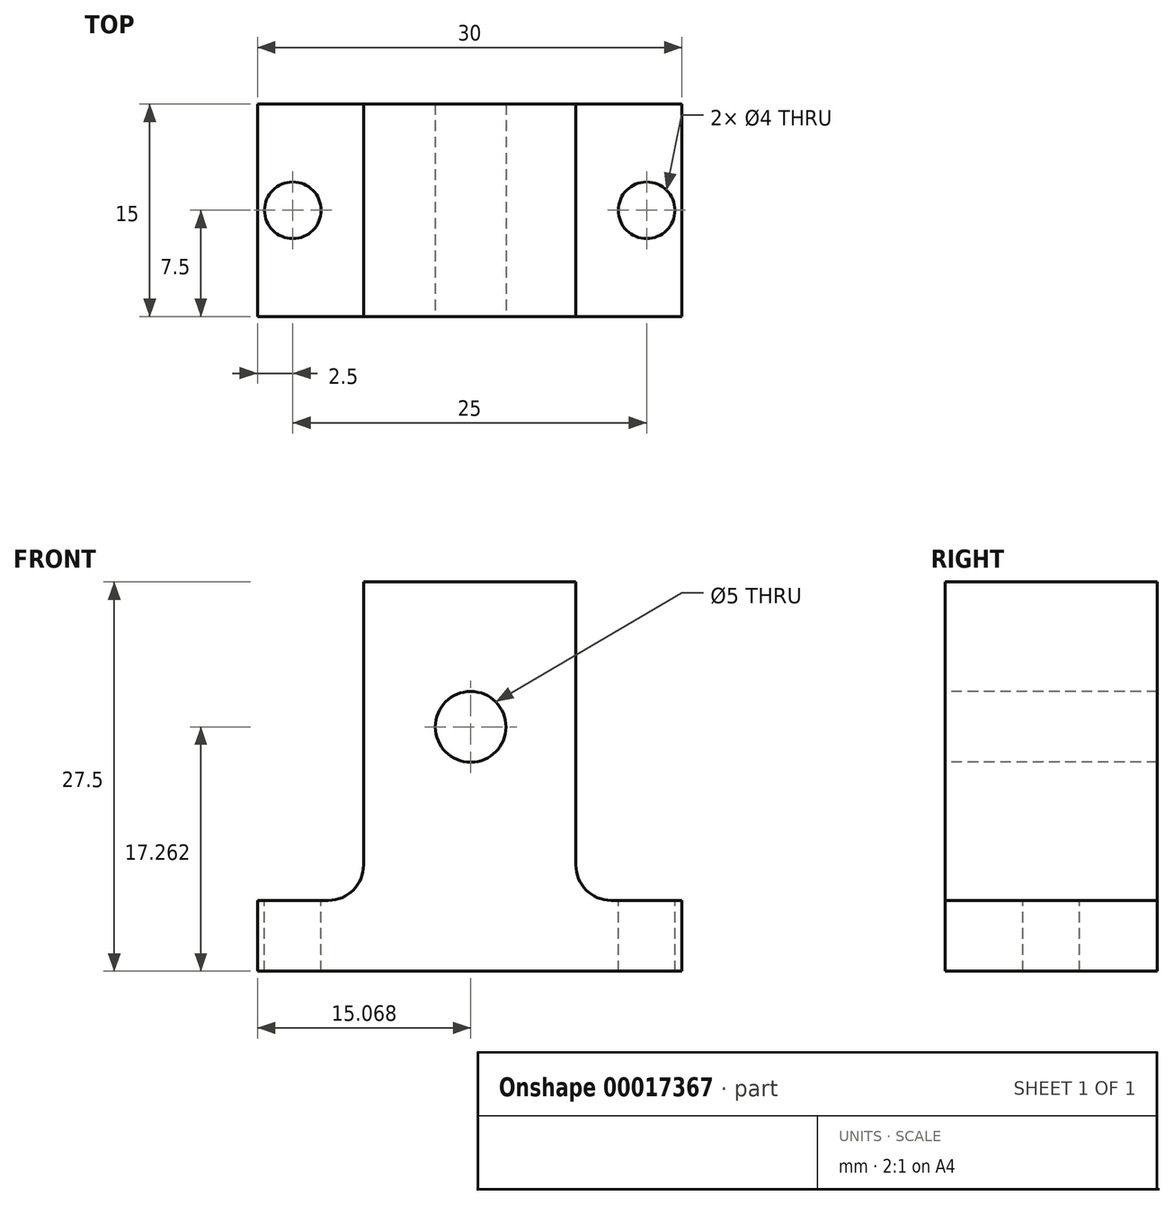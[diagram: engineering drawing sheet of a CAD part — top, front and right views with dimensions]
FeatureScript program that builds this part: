
annotation { "Feature Type Name" : "Feature", "Feature Type Description" : "" }
export const myFeature = defineFeature(function(context is Context, id is Id, definition is map)
    precondition{}
    {
        {
            var Q0;
            Q0=qCreatedBy(makeId("Front.planeOp"),FACE);
            var sketch = newSketch(context, id + "F0", { "sketchPlane" : qUnion([Q0])});
            skLineSegment(sketch, "E0", {"start": v(-35, -18.2) * mm, "end": v(-5, -18.2) * mm});
            skLineSegment(sketch, "E1", {"start": v(-5, -18.2) * mm, "end": v(-5, -13.2) * mm});
            skLineSegment(sketch, "E2", {"start": v(-35, -18.2) * mm, "end": v(-35, -13.2) * mm});
            skLineSegment(sketch, "E3", {"start": v(-35, -13.2) * mm, "end": v(-30, -13.2) * mm});
            skLineSegment(sketch, "E4", {"start": v(-5, -13.2) * mm, "end": v(-10, -13.2) * mm});
            skLineSegment(sketch, "E5", {"start": v(-12.5, -10.7) * mm, "end": v(-12.5, 9.3) * mm});
            skLineSegment(sketch, "E6", {"start": v(-27.5, -10.7) * mm, "end": v(-27.5, 9.3) * mm});
            skPoint(sketch, "E7.visualSharp", {"position": v(-27.5, -13.2) * mm});
            skArc(sketch, "E7.filletArc", {"start": v(-30, -13.2) * mm, "mid": v(-28.23, -12.48) * mm, "end": v(-27.5, -10.7) * mm});
            skPoint(sketch, "E8.visualSharp", {"position": v(-12.5, -13.2) * mm});
            skArc(sketch, "E8.filletArc", {"start": v(-12.5, -10.7) * mm, "mid": v(-11.77, -12.48) * mm, "end": v(-10, -13.2) * mm});
            skLineSegment(sketch, "E9", {"start": v(-27.5, 9.3) * mm, "end": v(-12.5, 9.3) * mm});
            skSolve(sketch);
        }
        {
            var Q0;
            Q0=makeQuery(id+"F0.imprint","IMPRINT",FACE,{"disambiguationData":[TD([[makeQuery(id+"F0.imprint","IMPRINT",EDGE,{"derivedFrom":sQuery(id+"F0.wireOp",EDGE,"E0")}),1.0]])]});
            extrude(context, id + "F1", {"entities" : qUnion([Q0]), "depth" : 15 * mm});
        }
        {
            var Q0;
            Q0=makeQuery(id+"F1.opExtrude","CAP_FACE",FACE,{"disambiguationData":[OSD([sQuery(id+"F0.wireOp",EDGE,"E0"),sQuery(id+"F0.wireOp",EDGE,"E1"),sQuery(id+"F0.wireOp",EDGE,"E2"),sQuery(id+"F0.wireOp",EDGE,"E3"),sQuery(id+"F0.wireOp",EDGE,"E4"),sQuery(id+"F0.wireOp",EDGE,"E5"),sQuery(id+"F0.wireOp",EDGE,"E6"),sQuery(id+"F0.wireOp",EDGE,"E7.filletArc"),sQuery(id+"F0.wireOp",EDGE,"E8.filletArc"),sQuery(id+"F0.wireOp",EDGE,"E9")])],"isStart":false});
            var sketch = newSketch(context, id + "F2", { "sketchPlane" : qUnion([Q0])});
            skSolve(sketch);
        }
        {
            var Q0;
            Q0=makeQuery(id+"F2.imprint","IMPRINT",FACE,{"disambiguationData":[TD([[makeQuery(id+"F2.imprint","IMPRINT",EDGE,{"derivedFrom":makeQuery(id+"F1.opExtrude","CAP_EDGE",EDGE,{"disambiguationData":[OSD([sQuery(id+"F0.wireOp",EDGE,"E0")])],"isStart":false})}),1.0]])]});
            var sketch = newSketch(context, id + "F3", { "sketchPlane" : qUnion([Q0])});
            skCircle(sketch, "E10", {"center": v(-19.93, -0.95) * mm, "radius": 2.5 * mm});
            skSolve(sketch);
        }
        {
            var Q0;
            Q0=makeQuery(id+"F3.imprint","IMPRINT",FACE,{"disambiguationData":[TD([[makeQuery(id+"F3.imprint","IMPRINT",EDGE,{"derivedFrom":sQuery(id+"F3.wireOp",EDGE,"E10")}),1.0]])]});
            var Q1;
            Q1=sQuery(id+"F3.wireOp",EDGE,"E10");
            extrude(context, id + "F4", {"entities" : qUnion([Q0]), "operationType" : NewBodyOperationType.REMOVE, "surfaceEntities" : qUnion([Q1]), "oppositeDirection" : true, "depth" : 25 * mm});
        }
        {
            var Q0;
            Q0=makeQuery(id+"F1.opExtrude","SWEPT_FACE",FACE,{"disambiguationData":[OSD([sQuery(id+"F0.wireOp",EDGE,"E4")])]});
            var sketch = newSketch(context, id + "F5", { "sketchPlane" : qUnion([Q0])});
            skCircle(sketch, "E11", {"center": v(-27.1, -7) * mm, "radius": 0.08 * mm});
            skCircle(sketch, "E12", {"center": v(-32.35, -7.31) * mm, "radius": 2 * mm});
            skCircle(sketch, "E13", {"center": v(-7.5, -7.5) * mm, "radius": 2 * mm});
            skSolve(sketch);
        }
        {
            var Q0;
            Q0=makeQuery(id+"F5.imprint","IMPRINT",FACE,{"disambiguationData":[TD([[makeQuery(id+"F5.imprint","IMPRINT",EDGE,{"derivedFrom":sQuery(id+"F5.wireOp",EDGE,"E13")}),1.0]])]});
            extrude(context, id + "F6", {"entities" : qUnion([Q0]), "operationType" : NewBodyOperationType.REMOVE, "oppositeDirection" : true, "depth" : 25 * mm});
        }
        {
            var Q0;
            Q0=makeQuery(id+"F1.opExtrude","SWEPT_FACE",FACE,{"disambiguationData":[OSD([sQuery(id+"F0.wireOp",EDGE,"E3")])]});
            var sketch = newSketch(context, id + "F7", { "sketchPlane" : qUnion([Q0])});
            skCircle(sketch, "E14", {"center": v(-32.5, -7.5) * mm, "radius": 2 * mm});
            skSolve(sketch);
        }
        {
            var Q0;
            Q0=makeQuery(id+"F7.imprint","IMPRINT",FACE,{"disambiguationData":[TD([[makeQuery(id+"F7.imprint","IMPRINT",EDGE,{"derivedFrom":sQuery(id+"F7.wireOp",EDGE,"E14")}),1.0]])]});
            extrude(context, id + "F8", {"entities" : qUnion([Q0]), "operationType" : NewBodyOperationType.REMOVE, "oppositeDirection" : true, "depth" : 25 * mm});
        }
    });
